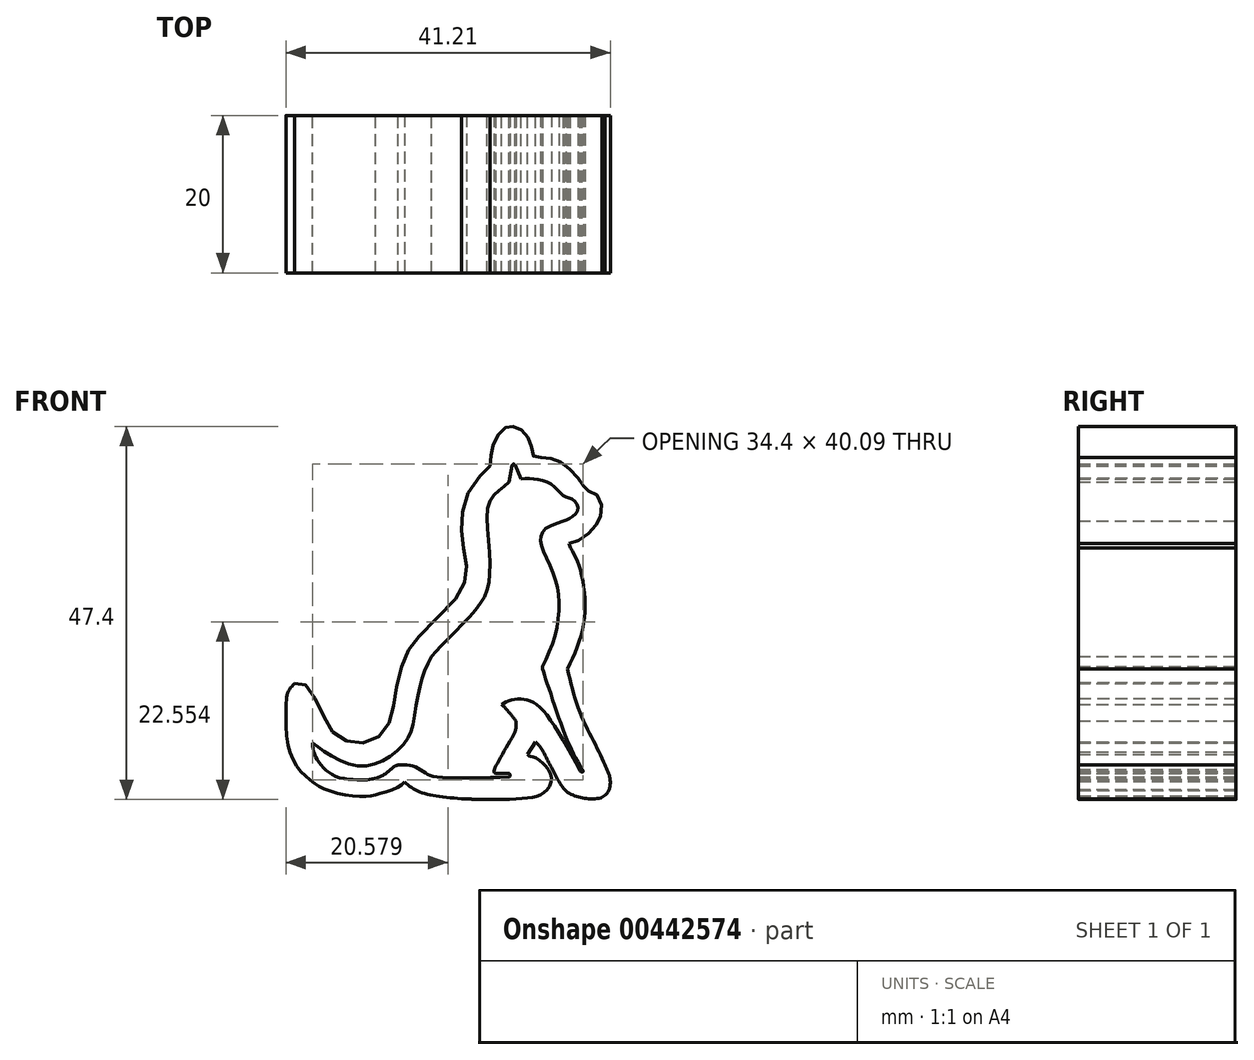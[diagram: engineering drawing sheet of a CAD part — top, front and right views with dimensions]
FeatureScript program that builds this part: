
annotation { "Feature Type Name" : "Feature", "Feature Type Description" : "" }
export const myFeature = defineFeature(function(context is Context, id is Id, definition is map)
    precondition{}
    {
        {
            var Q0;
            Q0=qCreatedBy(makeId("Front.planeOp"),FACE);
            var sketch = newSketch(context, id + "F0", { "sketchPlane" : qUnion([Q0])});
            skFitSpline(sketch, "E0", {"points": [v(-20.75, 46.1) * mm, v(-19.57, 43.44) * mm, v(-19.03, 36.92) * mm, v(-21.16, 30.73) * mm], "startDerivative": vector(5.02, -9.16) * mm, "endDerivative": vector(-7.33, -15.73) * mm});
            skFitSpline(sketch, "E1", {"points": [v(-16.4, 18.52) * mm, v(-17.76, 21.4) * mm, v(-19.68, 25.47) * mm, v(-21.16, 30.73) * mm], "startDerivative": vector(-4.44, 9.7) * mm, "endDerivative": vector(-3.4, 14.47) * mm});
            skFitSpline(sketch, "E2", {"points": [v(-16.4, 18.52) * mm, v(-15.75, 16.75) * mm, v(-16.03, 15.1) * mm, v(-17.03, 14.35) * mm, v(-18.65, 14.27) * mm, v(-20.16, 14.6) * mm, v(-21.51, 15.41) * mm, v(-23.37, 18.52) * mm, v(-24.24, 20.23) * mm], "startDerivative": vector(6.61, -13.65) * mm, "endDerivative": vector(-6.04, 11.6) * mm});
            skFitSpline(sketch, "E3", {"points": [v(-24.24, 20.23) * mm, v(-24.8, 21.05) * mm, v(-25.21, 21.45) * mm], "startDerivative": vector(-0.98, 1.6) * mm, "endDerivative": vector(-0.95, 0.8) * mm});
            skLineSegment(sketch, "E4", {"start": v(-25.21, 21.45) * mm, "end": v(-26.23, 19.88) * mm});
            skFitSpline(sketch, "E5", {"points": [v(-26.23, 19.88) * mm, v(-25.96, 19.65) * mm, v(-25.45, 19.54) * mm, v(-24.12, 18.6) * mm, v(-23.23, 17.05) * mm, v(-23.75, 15.38) * mm, v(-25.18, 14.54) * mm, v(-27.98, 14.21) * mm, v(-33.57, 14.2) * mm, v(-38.19, 14.67) * mm, v(-40.48, 15.37) * mm, v(-41.86, 16.4) * mm], "startDerivative": vector(6.47, -7.05) * mm, "endDerivative": vector(-15.26, 13.37) * mm});
            skFitSpline(sketch, "E6", {"points": [v(-41.86, 16.4) * mm, v(-42.9, 15.63) * mm, v(-45.02, 14.9) * mm, v(-46.3, 14.6) * mm, v(-48.82, 14.66) * mm, v(-52.05, 15.5) * mm, v(-53.58, 16.4) * mm, v(-55.34, 18.1) * mm, v(-56.63, 21.04) * mm, v(-56.93, 23.9) * mm, v(-56.87, 26.78) * mm, v(-56.49, 28.14) * mm, v(-55.83, 28.88) * mm], "startDerivative": vector(-13.32, -12.41) * mm, "endDerivative": vector(12.85, 11.74) * mm});
            skPoint(sketch, "E7.1.internal.orphan", {"position": v(-54.74, 28.88) * mm});
            skFitSpline(sketch, "E8", {"points": [v(-55.83, 28.88) * mm, v(-54.74, 28.88) * mm, v(-53.69, 27.8) * mm, v(-52.18, 24.84) * mm, v(-50.9, 22.66) * mm, v(-48.97, 21.51) * mm, v(-46.7, 21.44) * mm, v(-44.66, 22.57) * mm, v(-43.51, 24.75) * mm, v(-43.08, 27.37) * mm, v(-42.35, 30.62) * mm, v(-41.26, 33.3) * mm, v(-39.65, 35.3) * mm, v(-35.54, 39.46) * mm, v(-34.12, 42.02) * mm, v(-34.03, 44.43) * mm, v(-34.5, 46.94) * mm, v(-34.6, 49.66) * mm, v(-34, 52.6) * mm, v(-32.07, 55.52) * mm, v(-31.02, 56.53) * mm], "startDerivative": vector(35.2, 5.58) * mm, "endDerivative": vector(25.64, 22.49) * mm});
            skFitSpline(sketch, "E9", {"points": [v(-31.02, 56.53) * mm, v(-30.84, 58.19) * mm, v(-30.43, 59.67) * mm, v(-29.3, 61.22) * mm, v(-28.41, 61.56) * mm, v(-27.3, 61.3) * mm, v(-26.34, 60.34) * mm, v(-25.72, 58.97) * mm, v(-25.47, 57.76) * mm, v(-24.6, 57.6) * mm, v(-23.15, 57.45) * mm, v(-21.76, 56.84) * mm, v(-20.21, 55.45) * mm, v(-19.2, 54.08) * mm, v(-18.73, 53.43) * mm, v(-17.65, 53.02) * mm, v(-16.82, 51.6) * mm, v(-17.14, 49.77) * mm, v(-17.9, 48.6) * mm, v(-19.52, 47.16) * mm, v(-21, 46.71) * mm], "startDerivative": vector(2.98, 31.69) * mm, "endDerivative": vector(-28.55, -4.86) * mm});
            skFitSpline(sketch, "E10", {"points": [v(-20.75, 46.1) * mm, v(-21, 46.71) * mm], "startDerivative": vector(-0.25, 0.6) * mm, "endDerivative": vector(-0.25, 0.6) * mm});
            skFitSpline(sketch, "E11", {"points": [v(-38.43, 32.3) * mm, v(-37.07, 33.8) * mm, v(-34.24, 36.7) * mm, v(-32.2, 39.1) * mm, v(-31.34, 40.91) * mm, v(-31.02, 43.87) * mm, v(-31.34, 48.98) * mm, v(-31.02, 52.13) * mm, v(-29.86, 53.43) * mm, v(-28.62, 54.48) * mm], "startDerivative": vector(12.75, 14.38) * mm, "endDerivative": vector(14.38, 12.3) * mm});
            skLineSegment(sketch, "E12", {"start": v(-28.62, 54.48) * mm, "end": v(-28.2, 56.6) * mm});
            skPoint(sketch, "E13.visualSharp", {"position": v(-28.12, 56.97) * mm});
            skArc(sketch, "E13.filletArc", {"start": v(-27.86, 56.7) * mm, "mid": v(-28.06, 56.75) * mm, "end": v(-28.2, 56.6) * mm});
            skLineSegment(sketch, "E14", {"start": v(-27.86, 56.7) * mm, "end": v(-27.1, 54.9) * mm});
            skFitSpline(sketch, "E15", {"points": [v(-38.43, 32.3) * mm, v(-39.43, 30.16) * mm, v(-40.16, 27.43) * mm, v(-40.8, 23.75) * mm, v(-41.46, 21.87) * mm, v(-43.46, 19.8) * mm, v(-46.03, 18.57) * mm, v(-48.92, 18.67) * mm, v(-51.94, 20.16) * mm, v(-53.56, 21.33) * mm], "startDerivative": vector(-10.35, -20.34) * mm, "endDerivative": vector(-15.4, 11.87) * mm});
            skFitSpline(sketch, "E16", {"points": [v(-28.5, 17.02) * mm, v(-28.5, 17.4) * mm, v(-28.98, 17.49) * mm, v(-30.27, 17.49) * mm], "startDerivative": vector(0.36, 1.81) * mm, "endDerivative": vector(-3.01, 0.01) * mm});
            skFitSpline(sketch, "E17", {"points": [v(-30.27, 17.49) * mm, v(-30.47, 17.63) * mm, v(-30.47, 17.93) * mm, v(-30.11, 18.69) * mm, v(-28.92, 20.77) * mm, v(-27.8, 22.83) * mm, v(-27.68, 23.56) * mm, v(-27.72, 24.16) * mm], "startDerivative": vector(-3.25, 1.61) * mm, "endDerivative": vector(-0.48, 5.19) * mm});
            skFitSpline(sketch, "E18", {"points": [v(-27.72, 24.16) * mm, v(-28.86, 25.55) * mm, v(-29.52, 26.22) * mm], "startDerivative": vector(-2.07, 2.62) * mm, "endDerivative": vector(-1.49, 1.43) * mm});
            skFitSpline(sketch, "E19", {"points": [v(-29.52, 26.22) * mm, v(-28.74, 26.65) * mm, v(-27.4, 26.92) * mm, v(-26, 26.7) * mm, v(-24.13, 25.31) * mm, v(-19.55, 17.78) * mm], "startDerivative": vector(5.86, 3.81) * mm, "endDerivative": vector(12.85, -23.7) * mm});
            skFitSpline(sketch, "E20", {"points": [v(-19.55, 17.78) * mm, v(-19.36, 17.65) * mm, v(-19.16, 17.7) * mm, v(-19.32, 18) * mm], "startDerivative": vector(0.52, -0.5) * mm, "endDerivative": vector(-0.7, 0.93) * mm});
            skFitSpline(sketch, "E21", {"points": [v(-19.32, 18) * mm, v(-21.08, 21.42) * mm, v(-23.32, 27.67) * mm, v(-24.32, 30.77) * mm, v(-24.34, 31.06) * mm], "startDerivative": vector(-6.2, 10.72) * mm, "endDerivative": vector(0.14, 2.81) * mm});
            skFitSpline(sketch, "E22", {"points": [v(-24.34, 31.06) * mm, v(-22.78, 34.87) * mm, v(-22.24, 39.27) * mm, v(-22.86, 42.6) * mm, v(-24.32, 46) * mm, v(-24.58, 47.45) * mm, v(-24.03, 48.5) * mm, v(-21.67, 49.53) * mm], "startDerivative": vector(10.28, 21.25) * mm, "endDerivative": vector(20.44, 6.37) * mm});
            skFitSpline(sketch, "E23", {"points": [v(-21.67, 49.53) * mm, v(-20.53, 50.09) * mm, v(-19.8, 51.22) * mm, v(-20.62, 52.32) * mm, v(-21.67, 52.71) * mm, v(-22.92, 54) * mm, v(-25.04, 54.85) * mm, v(-27.1, 54.9) * mm], "startDerivative": vector(9.05, 3.36) * mm, "endDerivative": vector(-12.36, -0.54) * mm});
            skLineSegment(sketch, "E24", {"start": v(-30.36, 14.16) * mm, "end": v(-61.82, 14.16) * mm});
            skLineSegment(sketch, "E25", {"start": v(-30.36, 14.16) * mm, "end": v(-11.32, 14.16) * mm});
            skFitSpline(sketch, "E26", {"points": [v(-21.51, 15.41) * mm, v(-20.72, 14.74) * mm, v(-19.46, 14.28) * mm, v(-18.03, 14.16) * mm, v(-16.96, 14.3) * mm, v(-16.28, 14.67) * mm, v(-16.03, 15.1) * mm], "startDerivative": vector(4.22, -4.25) * mm, "endDerivative": vector(1.62, 3.8) * mm});
            skLineSegment(sketch, "E27", {"start": v(-33.57, 14.2) * mm, "end": v(-33.57, 13.95) * mm});
            skLineSegment(sketch, "E28", {"start": v(-33.57, 14.2) * mm, "end": v(-33.57, 14.49) * mm});
            skFitSpline(sketch, "E29", {"points": [v(-41.86, 16.4) * mm, v(-43.27, 15.2) * mm, v(-45.07, 14.49) * mm, v(-47.76, 14.16) * mm, v(-50.72, 14.49) * mm, v(-53.2, 15.5) * mm, v(-54.64, 16.93) * mm], "startDerivative": vector(-9.07, -8.9) * mm, "endDerivative": vector(-8.22, 9.85) * mm});
            skFitSpline(sketch, "E30", {"points": [v(-56.63, 21.04) * mm, v(-56.2, 19.4) * mm, v(-55.6, 17.86) * mm, v(-54.36, 16.21) * mm, v(-52.62, 15.16) * mm], "startDerivative": vector(1.77, -9.26) * mm, "endDerivative": vector(6.93, -3.4) * mm});
            skFitSpline(sketch, "E31", {"points": [v(-53.56, 21.33) * mm, v(-53.33, 19.98) * mm, v(-52.35, 18.42) * mm, v(-50.46, 17.04) * mm, v(-47.33, 16.67) * mm, v(-45.98, 16.76) * mm, v(-44.04, 17.3) * mm, v(-42.64, 17.71) * mm, v(-41.43, 17.73) * mm], "startDerivative": vector(0.9, -12.3) * mm, "endDerivative": vector(11.87, -0.67) * mm});
            skFitSpline(sketch, "E32", {"points": [v(-28.5, 17.02) * mm, v(-37.82, 17.02) * mm, v(-39.16, 17.5) * mm, v(-40.2, 18.13) * mm, v(-41.33, 18.53) * mm, v(-42.71, 18.53) * mm], "startDerivative": vector(-28.6, -0.96) * mm, "endDerivative": vector(-9.18, -0.6) * mm});
            skFitSpline(sketch, "E33", {"points": [v(-45.98, 16.76) * mm, v(-44.82, 17.11) * mm, v(-43.66, 17.94) * mm, v(-43.1, 18.37) * mm, v(-42.71, 18.53) * mm], "startDerivative": vector(3.97, 0.8) * mm, "endDerivative": vector(2.24, 0.73) * mm});
            skSolve(sketch);
        }
        {
            var Q0;
            Q0=makeQuery(id+"F0.imprint","IMPRINT",FACE,{"disambiguationData":[TD([[makeQuery(id+"F0.imprint","IMPRINT",EDGE,{"derivedFrom":sQuery(id+"F0.wireOp",EDGE,"E0")}),-1.0]])]});
            extrude(context, id + "F1", {"entities" : qUnion([Q0]), "depth" : 20 * mm});
        }
    });
